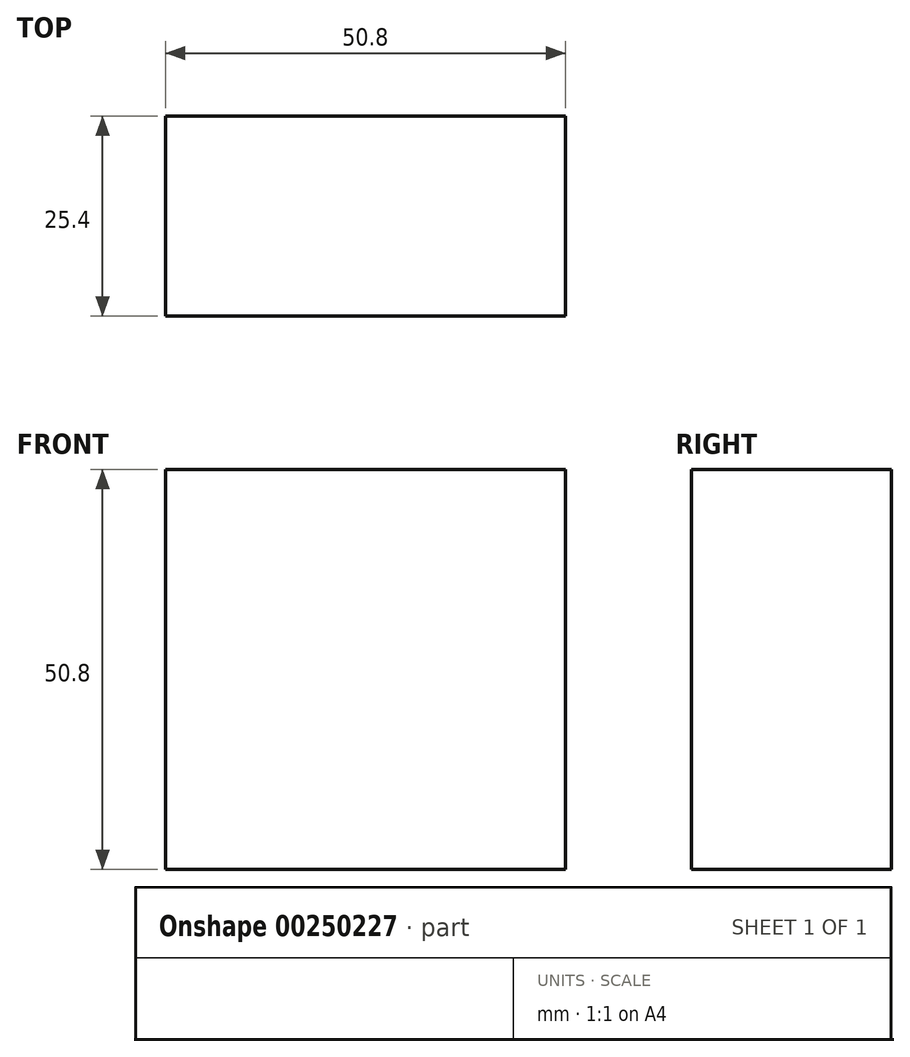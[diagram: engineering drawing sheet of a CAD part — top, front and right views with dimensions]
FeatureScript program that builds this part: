
annotation { "Feature Type Name" : "Feature", "Feature Type Description" : "" }
export const myFeature = defineFeature(function(context is Context, id is Id, definition is map)
    precondition{}
    {
        {
            var Q0;
            Q0=qCreatedBy(makeId("Front.planeOp"),FACE);
            var sketch = newSketch(context, id + "F0", { "sketchPlane" : qUnion([Q0])});
            skLineSegment(sketch, "E0.bottom", {"start": v(25.4, 25.4) * mm, "end": v(-25.4, 25.4) * mm});
            skLineSegment(sketch, "E0.top", {"start": v(25.4, -25.4) * mm, "end": v(-25.4, -25.4) * mm});
            skLineSegment(sketch, "E0.left", {"start": v(25.4, 25.4) * mm, "end": v(25.4, -25.4) * mm});
            skLineSegment(sketch, "E0.right", {"start": v(-25.4, 25.4) * mm, "end": v(-25.4, -25.4) * mm});
            skPoint(sketch, "E0.middle", {"position": v(0, 0) * mm});
            skSolve(sketch);
        }
        {
            var Q0;
            Q0 = qSketchRegion(id + "F0", true);
            extrude(context, id + "F1", {"entities" : qUnion([Q0]), "endBound" : BoundingType.SYMMETRIC, "depth" : 25.4 * mm});
        }
    });
